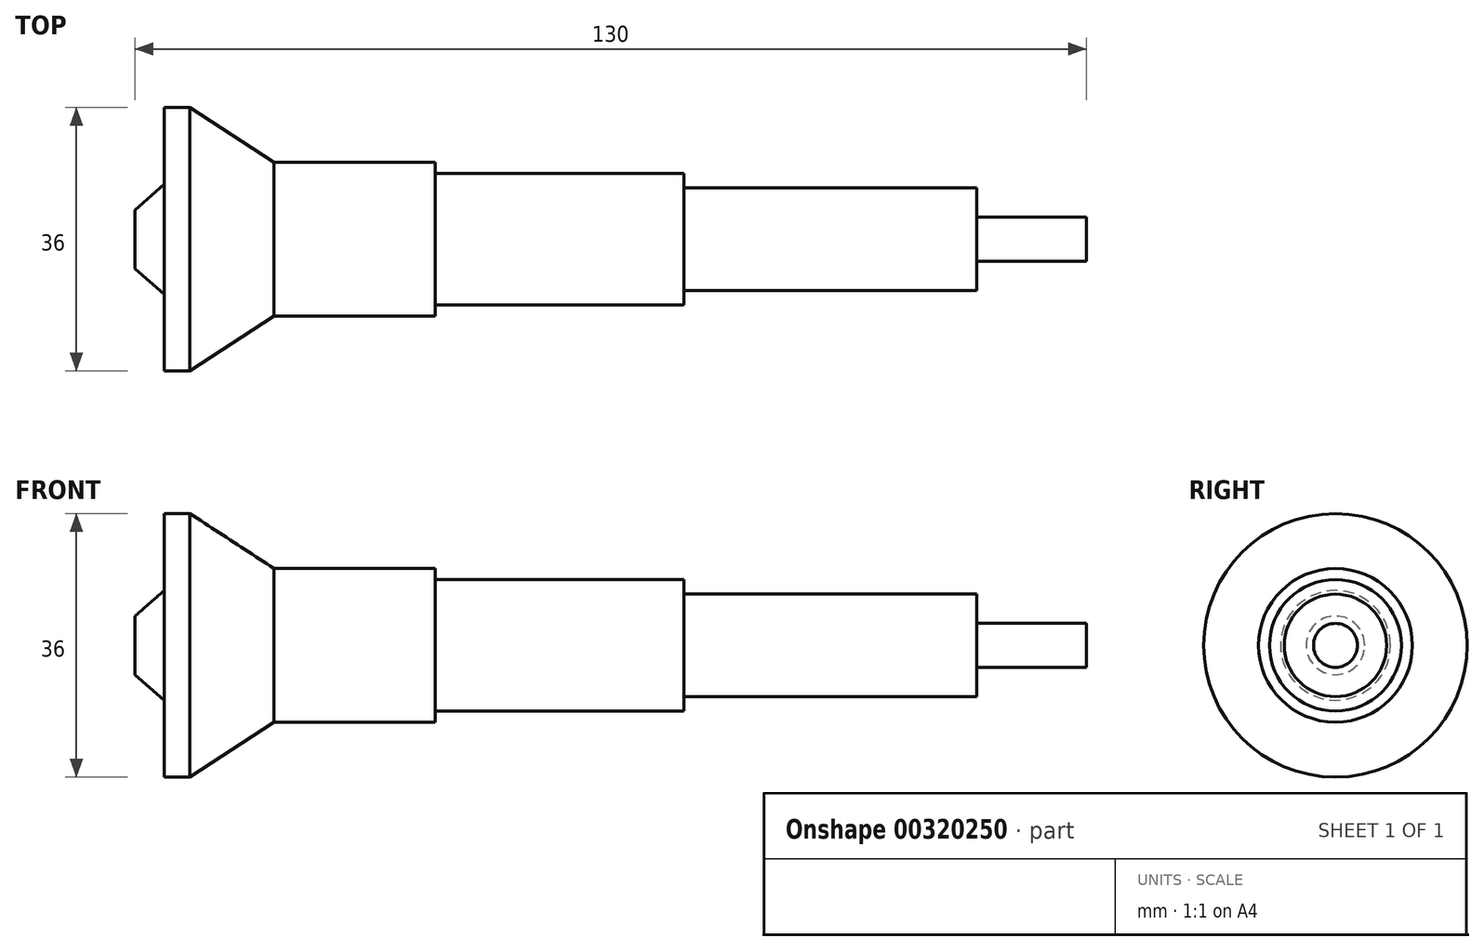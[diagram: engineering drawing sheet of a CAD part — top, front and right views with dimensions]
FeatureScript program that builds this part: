
annotation { "Feature Type Name" : "Feature", "Feature Type Description" : "" }
export const myFeature = defineFeature(function(context is Context, id is Id, definition is map)
    precondition{}
    {
        {
            var Q0;
            Q0=qCreatedBy(makeId("Front.planeOp"),FACE);
            var sketch = newSketch(context, id + "F0", { "sketchPlane" : qUnion([Q0])});
            skLineSegment(sketch, "E0", {"start": v(-115, 0) * mm, "end": v(15, 0) * mm});
            skLineSegment(sketch, "E1", {"start": v(-115, 0) * mm, "end": v(-115, 4) * mm});
            skLineSegment(sketch, "E2", {"start": v(-115, 4) * mm, "end": v(-111, 7.5) * mm});
            skLineSegment(sketch, "E3", {"start": v(-111, 7.5) * mm, "end": v(-111, 18) * mm});
            skLineSegment(sketch, "E4", {"start": v(-111, 18) * mm, "end": v(-107.5, 18) * mm});
            skLineSegment(sketch, "E5", {"start": v(-107.5, 18) * mm, "end": v(-96, 10.5) * mm});
            skLineSegment(sketch, "E6", {"start": v(-96, 10.5) * mm, "end": v(-74, 10.5) * mm});
            skLineSegment(sketch, "E7", {"start": v(-74, 10.5) * mm, "end": v(-74, 9) * mm});
            skLineSegment(sketch, "E8", {"start": v(-74, 9) * mm, "end": v(-40, 9) * mm});
            skLineSegment(sketch, "E9", {"start": v(0, 3) * mm, "end": v(15, 3) * mm});
            skLineSegment(sketch, "E10", {"start": v(15, 3) * mm, "end": v(15, 0) * mm});
            skLineSegment(sketch, "E11", {"start": v(-40, 9) * mm, "end": v(-40, 7) * mm});
            skLineSegment(sketch, "E12", {"start": v(-40, 7) * mm, "end": v(0, 7) * mm});
            skLineSegment(sketch, "E13", {"start": v(0, 7) * mm, "end": v(0, 3) * mm});
            skLineSegment(sketch, "E14", {"start": v(0, 3) * mm, "end": v(0, 0) * mm, "construction": true});
            skSolve(sketch);
        }
        {
            var Q0;
            Q0=makeQuery(id+"F0.imprint","IMPRINT",FACE,{"disambiguationData":[TD([[makeQuery(id+"F0.imprint","IMPRINT",EDGE,{"derivedFrom":sQuery(id+"F0.wireOp",EDGE,"E0")}),1.0]])]});
            var Q1;
            Q1=sQuery(id+"F0.wireOp",EDGE,"E0");
            revolve(context, id + "F1", {"entities" : qUnion([Q0]), "axis" : qUnion([Q1]), "revolveType" : RevolveType.FULL});
        }
    });
